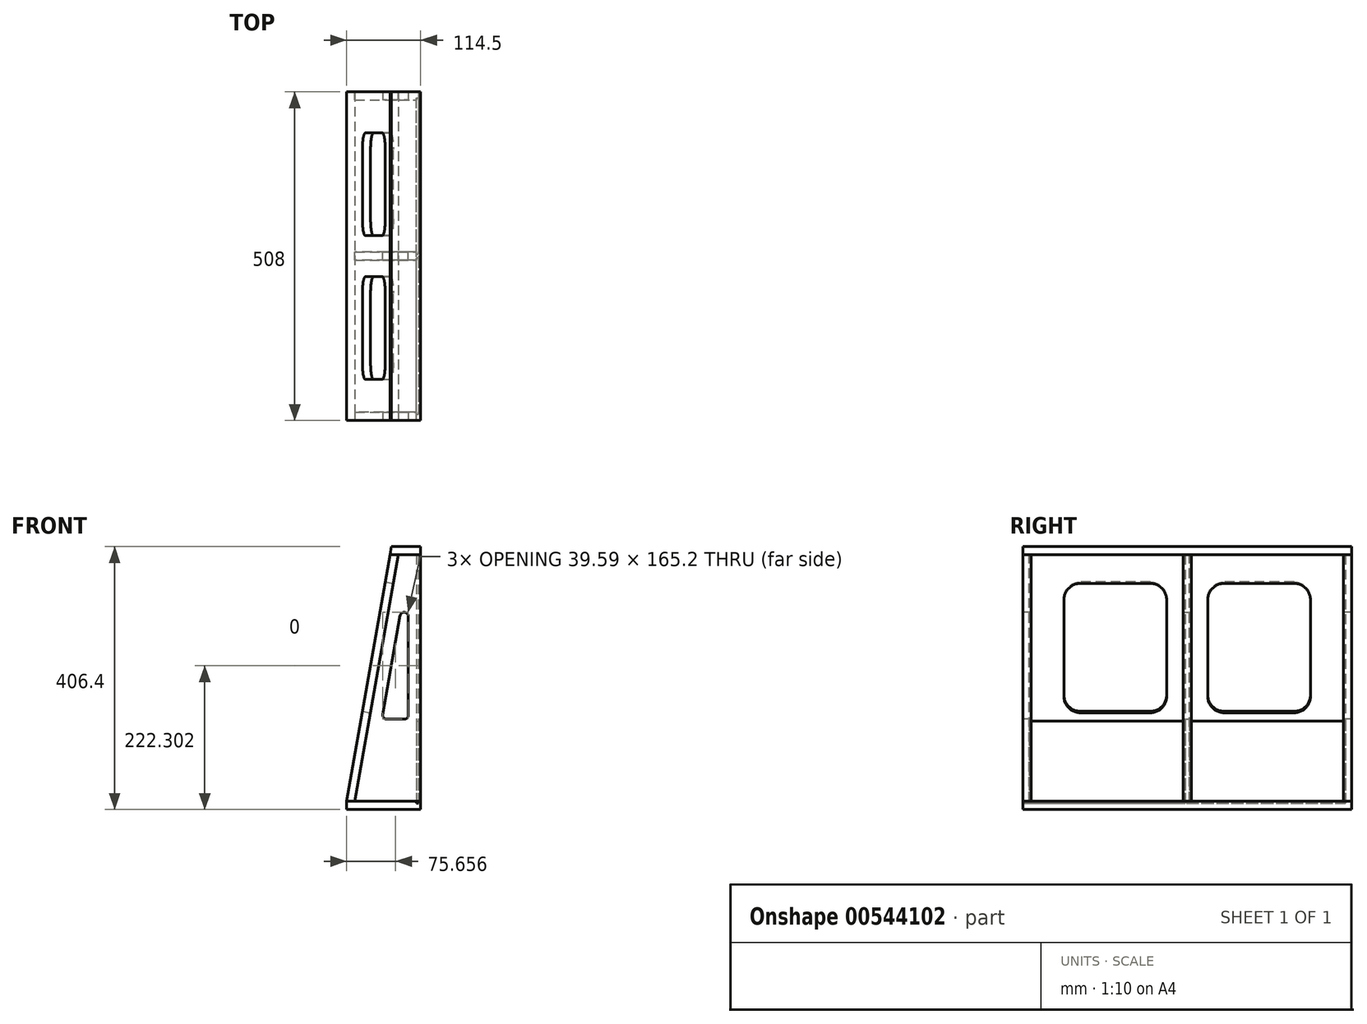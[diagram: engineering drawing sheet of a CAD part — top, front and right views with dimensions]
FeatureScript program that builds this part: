
annotation { "Feature Type Name" : "Feature", "Feature Type Description" : "" }
export const myFeature = defineFeature(function(context is Context, id is Id, definition is map)
    precondition{}
    {
        {
            var Q0;
            Q0=qCreatedBy(makeId("Front.planeOp"),FACE);
            var sketch = newSketch(context, id + "F0", { "sketchPlane" : qUnion([Q0])});
            skLineSegment(sketch, "E0", {"start": v(0, 0) * mm, "end": v(101.6, 0) * mm});
            skLineSegment(sketch, "E1", {"start": v(101.6, 0) * mm, "end": v(101.6, 381) * mm});
            skLineSegment(sketch, "E2", {"start": v(101.6, 381) * mm, "end": v(67.18, 381) * mm});
            skLineSegment(sketch, "E3", {"start": v(67.18, 381) * mm, "end": v(0, 0) * mm});
            skSolve(sketch);
        }
        {
            var Q0;
            Q0 = qSketchRegion(id + "F0", true);
            extrude(context, id + "F1", {"entities" : qUnion([Q0]), "oppositeDirection" : true, "depth" : 12.7 * mm, "offsetDistance" : 25.4 * mm});
        }
        {
            var Q0;
            Q0=makeQuery(id+"F1.opExtrude","CAP_FACE",FACE,{"disambiguationData":[OSD([sQuery(id+"F0.wireOp",EDGE,"E0"),sQuery(id+"F0.wireOp",EDGE,"E1"),sQuery(id+"F0.wireOp",EDGE,"E2"),sQuery(id+"F0.wireOp",EDGE,"E3")])],"isStart":true});
            var sketch = newSketch(context, id + "F2", { "sketchPlane" : qUnion([Q0])});
            skLineSegment(sketch, "E4.bottom", {"start": v(101.6, 0) * mm, "end": v(-12.7, 0) * mm});
            skLineSegment(sketch, "E4.top", {"start": v(101.6, -12.7) * mm, "end": v(-12.7, -12.7) * mm});
            skLineSegment(sketch, "E4.left", {"start": v(101.6, 0) * mm, "end": v(101.6, -12.7) * mm});
            skLineSegment(sketch, "E4.right", {"start": v(-12.7, 0) * mm, "end": v(-12.7, -12.7) * mm});
            skSolve(sketch);
        }
        {
            var Q0;
            Q0 = qSketchRegion(id + "F2", true);
            extrude(context, id + "F3", {"entities" : qUnion([Q0]), "oppositeDirection" : true, "depth" : 508 * mm, "offsetDistance" : 25.4 * mm});
        }
        {
            var Q0;
            Q0=makeQuery(id+"F3.opExtrude","CAP_FACE",FACE,{"disambiguationData":[OSD([sQuery(id+"F2.wireOp",EDGE,"E4.bottom"),sQuery(id+"F2.wireOp",EDGE,"E4.top"),sQuery(id+"F2.wireOp",EDGE,"E4.left"),sQuery(id+"F2.wireOp",EDGE,"E4.right")])],"isStart":false});
            var sketch = newSketch(context, id + "F4", { "sketchPlane" : qUnion([Q0])});
            skLineSegment(sketch, "E5.0.0", {"start": v(-67.18, 381) * mm, "end": v(-101.6, 381) * mm});
            skLineSegment(sketch, "E5.0.1", {"start": v(-101.6, 381) * mm, "end": v(-101.6, 0) * mm});
            skLineSegment(sketch, "E5.0.2", {"start": v(-101.6, 0) * mm, "end": v(0, 0) * mm});
            skLineSegment(sketch, "E5.0.3", {"start": v(0, 0) * mm, "end": v(-67.18, 381) * mm});
            skSolve(sketch);
        }
        {
            var Q0;
            Q0 = qSketchRegion(id + "F4", true);
            extrude(context, id + "F5", {"entities" : qUnion([Q0]), "oppositeDirection" : true, "depth" : 12.7 * mm, "offsetDistance" : 25.4 * mm});
        }
        {
            var Q0;
            Q0=makeQuery(id+"F1.opExtrude","CAP_FACE",FACE,{"disambiguationData":[OSD([sQuery(id+"F0.wireOp",EDGE,"E0"),sQuery(id+"F0.wireOp",EDGE,"E1"),sQuery(id+"F0.wireOp",EDGE,"E2"),sQuery(id+"F0.wireOp",EDGE,"E3")])],"isStart":true});
            var sketch = newSketch(context, id + "F6", { "sketchPlane" : qUnion([Q0])});
            skLineSegment(sketch, "E6", {"start": v(67.18, 381) * mm, "end": v(54.28, 381) * mm});
            skLineSegment(sketch, "E7", {"start": v(0, 0) * mm, "end": v(-12.9, 0) * mm});
            skLineSegment(sketch, "E8", {"start": v(54.28, 381) * mm, "end": v(-12.9, 0) * mm});
            skSolve(sketch);
        }
        {
            var Q0;
            Q0 = qSketchRegion(id + "F6", true);
            var Q1;
            Q1=makeQuery(id+"F6.imprint","IMPRINT",FACE,{"disambiguationData":[TD([[makeQuery(id+"F6.imprint","IMPRINT",EDGE,{"derivedFrom":sQuery(id+"F6.wireOp",EDGE,"E6")}),1.0]])]});
            var Q2;
            Q2=makeQuery(id+"F5.opExtrude","CAP_FACE",FACE,{"disambiguationData":[OSD([sQuery(id+"F4.wireOp",EDGE,"E5.0.0"),sQuery(id+"F4.wireOp",EDGE,"E5.0.1"),sQuery(id+"F4.wireOp",EDGE,"E5.0.2"),sQuery(id+"F4.wireOp",EDGE,"E5.0.3")])],"isStart":true});
            extrude(context, id + "F7", {"entities" : qUnion([Q0, Q1]), "endBound" : BoundingType.UP_TO_SURFACE, "oppositeDirection" : true, "depth" : 25.4 * mm, "endBoundEntityFace" : qUnion([Q2]), "offsetDistance" : 25.4 * mm});
        }
        {
            var Q0;
            Q0=makeQuery(id+"F5.opExtrude","CAP_FACE",FACE,{"disambiguationData":[OSD([sQuery(id+"F4.wireOp",EDGE,"E5.0.0"),sQuery(id+"F4.wireOp",EDGE,"E5.0.1"),sQuery(id+"F4.wireOp",EDGE,"E5.0.2"),sQuery(id+"F4.wireOp",EDGE,"E5.0.3")])],"isStart":true});
            var sketch = newSketch(context, id + "F8", { "sketchPlane" : qUnion([Q0])});
            skLineSegment(sketch, "E9.bottom", {"start": v(-101.6, 381) * mm, "end": v(-54.28, 381) * mm});
            skLineSegment(sketch, "E9.top", {"start": v(-101.6, 393.7) * mm, "end": v(-56.52, 393.7) * mm});
            skLineSegment(sketch, "E9.left", {"start": v(-101.6, 381) * mm, "end": v(-101.6, 393.7) * mm});
            skLineSegment(sketch, "E10", {"start": v(-54.28, 381) * mm, "end": v(-56.52, 393.7) * mm});
            skSolve(sketch);
        }
        {
            var Q0;
            Q0 = qSketchRegion(id + "F8", true);
            var Q1;
            Q1=makeQuery(id+"F1.opExtrude","CAP_FACE",FACE,{"disambiguationData":[OSD([sQuery(id+"F0.wireOp",EDGE,"E0"),sQuery(id+"F0.wireOp",EDGE,"E1"),sQuery(id+"F0.wireOp",EDGE,"E2"),sQuery(id+"F0.wireOp",EDGE,"E3")])],"isStart":true});
            extrude(context, id + "F9", {"entities" : qUnion([Q0]), "endBound" : BoundingType.UP_TO_SURFACE, "oppositeDirection" : true, "depth" : 25.4 * mm, "endBoundEntityFace" : qUnion([Q1]), "offsetDistance" : 25.4 * mm});
        }
        {
            var Q0;
            Q0=makeQuery(id+"F1.opExtrude","CAP_FACE",FACE,{"disambiguationData":[OSD([sQuery(id+"F0.wireOp",EDGE,"E0"),sQuery(id+"F0.wireOp",EDGE,"E1"),sQuery(id+"F0.wireOp",EDGE,"E2"),sQuery(id+"F0.wireOp",EDGE,"E3")])],"isStart":false});
            var sketch = newSketch(context, id + "F10", { "sketchPlane" : qUnion([Q0])});
            skLineSegment(sketch, "E11.0", {"start": v(-98.42, 0) * mm, "end": v(-98.42, 390.53) * mm});
            skLineSegment(sketch, "E12.0", {"start": v(-95.25, 0) * mm, "end": v(-95.25, 390.53) * mm});
            skSolve(sketch);
        }
        {
            var Q0;
            Q0 = qSketchRegion(id + "F10", true);
            var Q1;
            {var subQ0=sQuery(id+"F10.wireOp",EDGE,"E11.0");Q1=makeQuery(id+"F10.imprint","IMPRINT",FACE,{"disambiguationData":[TD([[makeQuery(id+"F10.imprint","IMPRINT",EDGE,{"derivedFrom":subQ0}),-1.0]])]});}
            extrude(context, id + "F11", {"entities" : qUnion([Q0, Q1]), "operationType" : NewBodyOperationType.REMOVE, "oppositeDirection" : true, "depth" : 3.17 * mm, "offsetDistance" : 25.4 * mm});
        }
        {
            var Q0;
            Q0=makeQuery(id+"F5.opExtrude","CAP_FACE",FACE,{"disambiguationData":[OSD([sQuery(id+"F4.wireOp",EDGE,"E5.0.0"),sQuery(id+"F4.wireOp",EDGE,"E5.0.1"),sQuery(id+"F4.wireOp",EDGE,"E5.0.2"),sQuery(id+"F4.wireOp",EDGE,"E5.0.3")])],"isStart":false});
            var sketch = newSketch(context, id + "F12", { "sketchPlane" : qUnion([Q0])});
            skLineSegment(sketch, "E13.0", {"start": v(98.42, 390.53) * mm, "end": v(98.42, 0) * mm});
            skLineSegment(sketch, "E14.0", {"start": v(95.25, 390.53) * mm, "end": v(95.25, 0) * mm});
            skSolve(sketch);
        }
        {
            var Q0;
            Q0 = qSketchRegion(id + "F12", true);
            var Q1;
            {var subQ0=sQuery(id+"F12.wireOp",EDGE,"E13.0");Q1=makeQuery(id+"F12.imprint","IMPRINT",FACE,{"disambiguationData":[TD([[makeQuery(id+"F12.imprint","IMPRINT",EDGE,{"derivedFrom":subQ0}),-1.0]])]});}
            extrude(context, id + "F13", {"entities" : qUnion([Q0, Q1]), "operationType" : NewBodyOperationType.REMOVE, "oppositeDirection" : true, "depth" : 3.17 * mm, "offsetDistance" : 25.4 * mm});
        }
        {
            var Q0;
            {var subQ0=sQuery(id+"F4.wireOp",EDGE,"E5.0.0");var subQ1=sQuery(id+"F4.wireOp",EDGE,"E5.0.3");var subQ2=sQuery(id+"F4.wireOp",EDGE,"E5.0.2");Q0=makeQuery(id+"F13.boolean.opBoolean","SPLIT",FACE,{"disambiguationData":[TD([makeQuery(id+"F5.opExtrude","SWEPT_FACE",FACE,{"disambiguationData":[OSD([subQ1])]})])],"derivedFrom":makeQuery(id+"F5.opExtrude","CAP_FACE",FACE,{"disambiguationData":[OSD([subQ0,sQuery(id+"F4.wireOp",EDGE,"E5.0.1"),subQ2,subQ1])],"isStart":false})});}
            var Q1;
            {var subQ0=sQuery(id+"F0.wireOp",EDGE,"E0");var subQ1=sQuery(id+"F0.wireOp",EDGE,"E3");var subQ2=sQuery(id+"F0.wireOp",EDGE,"E2");Q1=makeQuery(id+"F11.boolean.opBoolean","SPLIT",FACE,{"disambiguationData":[TD([makeQuery(id+"F1.opExtrude","SWEPT_FACE",FACE,{"disambiguationData":[OSD([subQ1])]})])],"derivedFrom":makeQuery(id+"F1.opExtrude","CAP_FACE",FACE,{"disambiguationData":[OSD([subQ0,sQuery(id+"F0.wireOp",EDGE,"E1"),subQ2,subQ1])],"isStart":false})});}
            cPlane(context, id + "F14", {"entities" : qUnion([Q0, Q1]), "cplaneType" : CPlaneType.MID_PLANE, "offset" : 25.4 * mm, "width" : 152.4 * mm, "height" : 152.4 * mm});
        }
        {
            var Q0;
            Q0=qCreatedBy(id+"F14.planeOp",FACE);
            var sketch = newSketch(context, id + "F15", { "sketchPlane" : qUnion([Q0])});
            skLineSegment(sketch, "E15.0.2", {"start": v(0, 0) * mm, "end": v(67.18, 381) * mm});
            skLineSegment(sketch, "E16.0", {"start": v(43.05, 134.45) * mm, "end": v(69.95, 286.98) * mm});
            skLineSegment(sketch, "E16.2", {"start": v(82.55, 285.88) * mm, "end": v(82.55, 133.35) * mm});
            skLineSegment(sketch, "E17.0", {"start": v(76.2, 127) * mm, "end": v(49.3, 127) * mm});
            skPoint(sketch, "E18.visualSharp", {"position": v(82.55, 358.46) * mm});
            skArc(sketch, "E18.filletArc", {"start": v(82.55, 285.88) * mm, "mid": v(76.75, 292.2) * mm, "end": v(69.95, 286.98) * mm});
            skPoint(sketch, "E19.visualSharp", {"position": v(82.55, 127) * mm});
            skArc(sketch, "E19.filletArc", {"start": v(76.2, 127) * mm, "mid": v(80.7, 128.86) * mm, "end": v(82.55, 133.35) * mm});
            skPoint(sketch, "E20.visualSharp", {"position": v(41.74, 127) * mm});
            skArc(sketch, "E20.filletArc", {"start": v(43.05, 134.45) * mm, "mid": v(44.44, 129.27) * mm, "end": v(49.3, 127) * mm});
            skLineSegment(sketch, "E21.0", {"start": v(101.6, 381) * mm, "end": v(101.6, 0) * mm});
            skLineSegment(sketch, "E22", {"start": v(101.6, 0) * mm, "end": v(0, 0) * mm});
            skLineSegment(sketch, "E23", {"start": v(67.18, 381) * mm, "end": v(101.6, 381) * mm});
            skSolve(sketch);
        }
        {
            var Q0;
            Q0 = qSketchRegion(id + "F15", true);
            extrude(context, id + "F16", {"entities" : qUnion([Q0]), "endBound" : BoundingType.SYMMETRIC, "depth" : 12.7 * mm, "offsetDistance" : 25.4 * mm});
        }
        {
            var Q0;
            Q0=makeQuery(id+"F16.opExtrude","CAP_FACE",FACE,{"disambiguationData":[OSD([sQuery(id+"F15.wireOp",EDGE,"E15.0.2"),sQuery(id+"F15.wireOp",EDGE,"E16.0"),sQuery(id+"F15.wireOp",EDGE,"E16.2"),sQuery(id+"F15.wireOp",EDGE,"E17.0"),sQuery(id+"F15.wireOp",EDGE,"E18.filletArc"),sQuery(id+"F15.wireOp",EDGE,"E19.filletArc"),sQuery(id+"F15.wireOp",EDGE,"E20.filletArc"),sQuery(id+"F15.wireOp",EDGE,"E21.0"),sQuery(id+"F15.wireOp",EDGE,"E22"),sQuery(id+"F15.wireOp",EDGE,"E23")])],"isStart":false});
            var sketch = newSketch(context, id + "F17", { "sketchPlane" : qUnion([Q0])});
            skLineSegment(sketch, "E24.0", {"start": v(95.25, 381) * mm, "end": v(95.25, 0) * mm});
            skLineSegment(sketch, "E24.1", {"start": v(98.42, 381) * mm, "end": v(98.42, 0) * mm});
            skSolve(sketch);
        }
        {
            var Q0;
            Q0 = qSketchRegion(id + "F17", true);
            var Q1;
            {var subQ0=sQuery(id+"F17.wireOp",EDGE,"E24.0");Q1=makeQuery(id+"F17.imprint","IMPRINT",FACE,{"disambiguationData":[TD([[makeQuery(id+"F17.imprint","IMPRINT",EDGE,{"derivedFrom":subQ0}),1.0]])]});}
            extrude(context, id + "F18", {"entities" : qUnion([Q0, Q1]), "operationType" : NewBodyOperationType.REMOVE, "oppositeDirection" : true, "depth" : 3.17 * mm, "offsetDistance" : 25.4 * mm});
        }
        {
            var Q0;
            Q0=makeQuery(id+"F16.opExtrude","CAP_FACE",FACE,{"disambiguationData":[OSD([sQuery(id+"F15.wireOp",EDGE,"E15.0.2"),sQuery(id+"F15.wireOp",EDGE,"E16.0"),sQuery(id+"F15.wireOp",EDGE,"E16.2"),sQuery(id+"F15.wireOp",EDGE,"E17.0"),sQuery(id+"F15.wireOp",EDGE,"E18.filletArc"),sQuery(id+"F15.wireOp",EDGE,"E19.filletArc"),sQuery(id+"F15.wireOp",EDGE,"E20.filletArc"),sQuery(id+"F15.wireOp",EDGE,"E21.0"),sQuery(id+"F15.wireOp",EDGE,"E22"),sQuery(id+"F15.wireOp",EDGE,"E23")])],"isStart":true});
            var sketch = newSketch(context, id + "F19", { "sketchPlane" : qUnion([Q0])});
            skLineSegment(sketch, "E25.0.0", {"start": v(-98.42, 0) * mm, "end": v(-95.25, 0) * mm});
            skLineSegment(sketch, "E25.0.1", {"start": v(-95.25, 0) * mm, "end": v(-95.25, 381) * mm});
            skLineSegment(sketch, "E25.0.2", {"start": v(-95.25, 381) * mm, "end": v(-98.42, 381) * mm});
            skLineSegment(sketch, "E25.0.3", {"start": v(-98.42, 381) * mm, "end": v(-98.42, 0) * mm});
            skSolve(sketch);
        }
        {
            var Q0;
            Q0 = qSketchRegion(id + "F19", true);
            extrude(context, id + "F20", {"entities" : qUnion([Q0]), "operationType" : NewBodyOperationType.REMOVE, "oppositeDirection" : true, "depth" : 3.17 * mm, "offsetDistance" : 25.4 * mm});
        }
        {
            var Q0;
            Q0=makeQuery(id+"F3.opExtrude","SWEPT_FACE",FACE,{"disambiguationData":[OSD([sQuery(id+"F2.wireOp",EDGE,"E4.bottom")])]});
            var sketch = newSketch(context, id + "F21", { "sketchPlane" : qUnion([Q0])});
            skLineSegment(sketch, "E26", {"start": v(95.25, 498.48) * mm, "end": v(95.25, 9.53) * mm});
            skLineSegment(sketch, "E27", {"start": v(98.43, 9.53) * mm, "end": v(98.43, 498.48) * mm});
            skLineSegment(sketch, "E28", {"start": v(95.25, 498.48) * mm, "end": v(95.25, 508) * mm});
            skLineSegment(sketch, "E29", {"start": v(98.43, 498.48) * mm, "end": v(98.43, 508) * mm});
            skLineSegment(sketch, "E30.0", {"start": v(95.25, 508) * mm, "end": v(98.43, 508) * mm});
            skPoint(sketch, "E31.orphan", {"position": v(-12.7, 508) * mm});
            skPoint(sketch, "E32.orphan", {"position": v(101.6, 508) * mm});
            skLineSegment(sketch, "E33", {"start": v(95.25, 9.53) * mm, "end": v(95.25, 0) * mm});
            skLineSegment(sketch, "E34", {"start": v(98.43, 9.53) * mm, "end": v(98.43, 0) * mm});
            skLineSegment(sketch, "E35", {"start": v(98.43, 0) * mm, "end": v(95.25, 0) * mm});
            skSolve(sketch);
        }
        {
            var Q0;
            Q0 = qSketchRegion(id + "F21", true);
            extrude(context, id + "F22", {"entities" : qUnion([Q0]), "operationType" : NewBodyOperationType.REMOVE, "oppositeDirection" : true, "depth" : 3.17 * mm, "offsetDistance" : 25.4 * mm});
        }
        {
            var Q0;
            Q0=makeQuery(id+"F22.boolean.opBoolean","COPY",FACE,{"derivedFrom":makeQuery(id+"F22.opExtrude","CAP_FACE",FACE,{"disambiguationData":[OSD([sQuery(id+"F21.wireOp",EDGE,"E26"),sQuery(id+"F21.wireOp",EDGE,"E27"),sQuery(id+"F21.wireOp",EDGE,"E28"),sQuery(id+"F21.wireOp",EDGE,"E29"),sQuery(id+"F21.wireOp",EDGE,"E30.0"),sQuery(id+"F21.wireOp",EDGE,"E33"),sQuery(id+"F21.wireOp",EDGE,"E34"),sQuery(id+"F21.wireOp",EDGE,"E35")])],"isStart":false})});
            var sketch = newSketch(context, id + "F23", { "sketchPlane" : qUnion([Q0])});
            skLineSegment(sketch, "E36.0", {"start": v(95.25, 498.48) * mm, "end": v(98.42, 498.48) * mm});
            skLineSegment(sketch, "E37.0", {"start": v(95.25, 257.18) * mm, "end": v(98.42, 257.18) * mm});
            skLineSegment(sketch, "E37.1", {"start": v(95.25, 250.83) * mm, "end": v(98.42, 250.83) * mm});
            skLineSegment(sketch, "E38.0", {"start": v(98.42, 9.53) * mm, "end": v(95.25, 9.53) * mm});
            skLineSegment(sketch, "E39", {"start": v(95.25, 250.83) * mm, "end": v(95.25, 9.53) * mm});
            skLineSegment(sketch, "E40", {"start": v(98.42, 9.53) * mm, "end": v(98.42, 250.83) * mm});
            skLineSegment(sketch, "E41", {"start": v(95.25, 257.18) * mm, "end": v(95.25, 498.48) * mm});
            skLineSegment(sketch, "E42", {"start": v(98.42, 498.48) * mm, "end": v(98.42, 257.18) * mm});
            skSolve(sketch);
        }
        {
            var Q0;
            Q0 = qSketchRegion(id + "F23", true);
            extrude(context, id + "F24", {"entities" : qUnion([Q0]), "depth" : 127 * mm, "offsetDistance" : 25.4 * mm});
        }
        {
            var Q0;
            Q0=makeQuery(id+"F1.opExtrude","CAP_FACE",FACE,{"disambiguationData":[OSD([sQuery(id+"F0.wireOp",EDGE,"E0"),sQuery(id+"F0.wireOp",EDGE,"E1"),sQuery(id+"F0.wireOp",EDGE,"E2"),sQuery(id+"F0.wireOp",EDGE,"E3")])],"isStart":true});
            var sketch = newSketch(context, id + "F25", { "sketchPlane" : qUnion([Q0])});
            skLineSegment(sketch, "E43.0", {"start": v(43.05, 134.45) * mm, "end": v(69.95, 286.98) * mm});
            skArc(sketch, "E43.1", {"start": v(43.05, 134.45) * mm, "mid": v(44.44, 129.27) * mm, "end": v(49.3, 127) * mm});
            skLineSegment(sketch, "E43.2", {"start": v(76.2, 127) * mm, "end": v(49.3, 127) * mm});
            skArc(sketch, "E43.3", {"start": v(76.2, 127) * mm, "mid": v(80.7, 128.86) * mm, "end": v(82.55, 133.35) * mm});
            skLineSegment(sketch, "E43.4", {"start": v(82.55, 285.88) * mm, "end": v(82.55, 133.35) * mm});
            skArc(sketch, "E43.5", {"start": v(82.55, 285.88) * mm, "mid": v(76.75, 292.2) * mm, "end": v(69.95, 286.98) * mm});
            skSolve(sketch);
        }
        {
            var Q0;
            Q0 = qSketchRegion(id + "F25", true);
            extrude(context, id + "F26", {"entities" : qUnion([Q0]), "operationType" : NewBodyOperationType.REMOVE, "endBound" : BoundingType.THROUGH_ALL, "oppositeDirection" : true, "depth" : 25.4 * mm, "offsetDistance" : 25.4 * mm});
        }
        {
            var Q0;
            Q0=makeQuery(id+"F7.opExtrude","SWEPT_FACE",FACE,{"disambiguationData":[OSD([sQuery(id+"F0.wireOp",EDGE,"E3")])]});
            var sketch = newSketch(context, id + "F27", { "sketchPlane" : qUnion([Q0])});
            skLineSegment(sketch, "E44.0", {"start": v(88.9, 342.05) * mm, "end": v(196.85, 342.05) * mm});
            skLineSegment(sketch, "E45.0", {"start": v(222.25, 316.65) * mm, "end": v(222.25, 164.44) * mm});
            skLineSegment(sketch, "E46.0", {"start": v(63.5, 164.44) * mm, "end": v(63.5, 316.65) * mm});
            skLineSegment(sketch, "E47.0", {"start": v(285.75, 316.65) * mm, "end": v(285.75, 164.44) * mm});
            skLineSegment(sketch, "E48.0", {"start": v(444.5, 316.65) * mm, "end": v(444.5, 164.44) * mm});
            skLineSegment(sketch, "E49.0", {"start": v(196.85, 139.04) * mm, "end": v(88.9, 139.04) * mm});
            skLineSegment(sketch, "E49.1", {"start": v(419.1, 139.04) * mm, "end": v(311.15, 139.04) * mm});
            skArc(sketch, "E50.filletArc", {"start": v(88.9, 342.05) * mm, "mid": v(70.94, 334.61) * mm, "end": v(63.5, 316.65) * mm});
            skPoint(sketch, "E51.newPointB", {"position": v(9.53, 139.04) * mm});
            skArc(sketch, "E51.filletArc", {"start": v(63.5, 164.44) * mm, "mid": v(70.94, 146.47) * mm, "end": v(88.9, 139.04) * mm});
            skPoint(sketch, "E52.newPointA", {"position": v(250.83, 139.04) * mm});
            skArc(sketch, "E52.filletArc", {"start": v(196.85, 139.04) * mm, "mid": v(214.81, 146.47) * mm, "end": v(222.25, 164.44) * mm});
            skArc(sketch, "E53.filletArc", {"start": v(222.25, 316.65) * mm, "mid": v(214.81, 334.61) * mm, "end": v(196.85, 342.05) * mm});
            skLineSegment(sketch, "E54", {"start": v(311.15, 342.05) * mm, "end": v(419.1, 342.05) * mm});
            skArc(sketch, "E55.filletArc", {"start": v(311.15, 342.05) * mm, "mid": v(293.19, 334.61) * mm, "end": v(285.75, 316.65) * mm});
            skArc(sketch, "E56.filletArc", {"start": v(444.5, 316.65) * mm, "mid": v(437.06, 334.61) * mm, "end": v(419.1, 342.05) * mm});
            skPoint(sketch, "E57.newPointB", {"position": v(498.48, 139.04) * mm});
            skArc(sketch, "E57.filletArc", {"start": v(419.1, 139.04) * mm, "mid": v(437.06, 146.47) * mm, "end": v(444.5, 164.44) * mm});
            skPoint(sketch, "E58.newPointA", {"position": v(257.18, 139.04) * mm});
            skArc(sketch, "E58.filletArc", {"start": v(285.75, 164.44) * mm, "mid": v(293.19, 146.47) * mm, "end": v(311.15, 139.04) * mm});
            skSolve(sketch);
        }
        {
            var Q0;
            Q0 = qSketchRegion(id + "F27", true);
            extrude(context, id + "F28", {"entities" : qUnion([Q0]), "operationType" : NewBodyOperationType.REMOVE, "endBound" : BoundingType.THROUGH_ALL, "oppositeDirection" : true, "depth" : 25.4 * mm, "offsetDistance" : 25.4 * mm});
        }
    });
